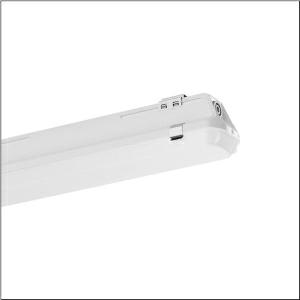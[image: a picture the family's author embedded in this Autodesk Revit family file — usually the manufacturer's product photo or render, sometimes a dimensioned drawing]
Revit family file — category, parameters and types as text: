
# Revit family: monsun_r__11_51fp107p460h_50c3
name_source: partatom
category: Lighting Fixtures
units: mm (PartAtom-declared; Revit-internal decimal feet)

## family parameters
Cut with Voids When Loaded = No
Host = Face
Light Source = No
Part Type = Normal
Room Calculation Point = No
Round Connector Dimension = Use Diameter
Shared = No

## types (1)
- Monsun® 11 (1 x LED, 5800 lm, 32.5 W, 4000K)
    Apparent Load = 33 VA
    CIE Flux Codes = 47 77 93 94 100
    Color Rendering = 80
    Color Temperature = 4000K
    Default Elevation = 1800 mm
    Description = Monsun® 11, damp-proof luminaire, chain hanger, primary optical cover: enclosure, of PMMA, light emission: direct distribution, primary light characteristic: symmetric, installation type: suspended mounting, surface-mounted, horizontal mounting, vertical mounting, LED, rated luminous flux: 5.800lm, luminous efficacy: 178lm/W, light colour: 840, colour temperature: 4000K, control gear: ECG, with terminal, 3-pole, max. 2.5mm², mains connection: 220..240V, AC, 50/60Hz, rated input power: 33W, luminaire housing, of glass-fibre reinforced polyester, uncoated, bright grey, incl. chain hanger, length: 1.590mm, width: 90mm, height: 88mm, clip for enclosure, of stainless steel (V2A), ceiling mounting element, of stainless steel (V2A), chain hanger, of stainless steel (V2A), protection rating (complete): IP66, insulation class (complete): insulation class I (protective earthing), certification: CE, ENEC, VDE, UKCA, protection symbol: D, impact resistance: IK04, permissible operating ambient temperature: -35..+40°C, standard: EN 50419, EN 60598-2-1, no direct snow, no direct sun, no direct rain, for indoor or canopied outdoor use, corresponds to IFS (International Featured Standards) requirements for safety and quality in the food industry, contact your sales advisor before using the luminaires in applications with unclear chemical exposure, large temperature fluctuations or condensation-forming humidity, LABS conformity tested according to VDMA 24364:2018-05, packaging unit: 1 piece
    Height = 89 mm
    Lamp = 1 x LED
    Lamp Light Flux = 5800 lm
    Lamp Power = 32.5 W
    Lamp count = 1
    Length = 1590 mm
    Luminous efficacy = 178 lm/W
    Manufacturer = Siteco
    ModVariant = No
    Model = 51FP107P460H
    Mounting Place = Ceiling
    Mounting Type = Surface mounted
    Number of Poles = 1
    OnlyDefault = Yes
    Power Factor = 1
    Product Name = Monsun® 11
    Product group = damp-proof luminaire
    ProductGroupID = 301
    Protection Class = Protection class I
    Protection Degree = IP 66
    RLX_Detail_Level = 1
    RLX_Emergency_Light_Flux = 0 lm
    RLX_Emergency_Type = 0
    RLX_Emergency_Type_DB = No
    RlxData = <blob elided: 88453 chars, md5=48bb642c>
    Socket = socket
    Standby Power = 0 W
    System Light Flux = 5800 lm
    System Power = 33 W
    Type Comments = Product without accessories
    Type Image = l_1004748.jpg
    URL = http://relux.com
    VarID = ---
    Voltage = 0 V
    Weight = 0.00 kg
    Width = 90 mm

## geometry (parser evidence)
native form markers: Blend x4, Sweep x13
no freeform markers — native parametric forms only
